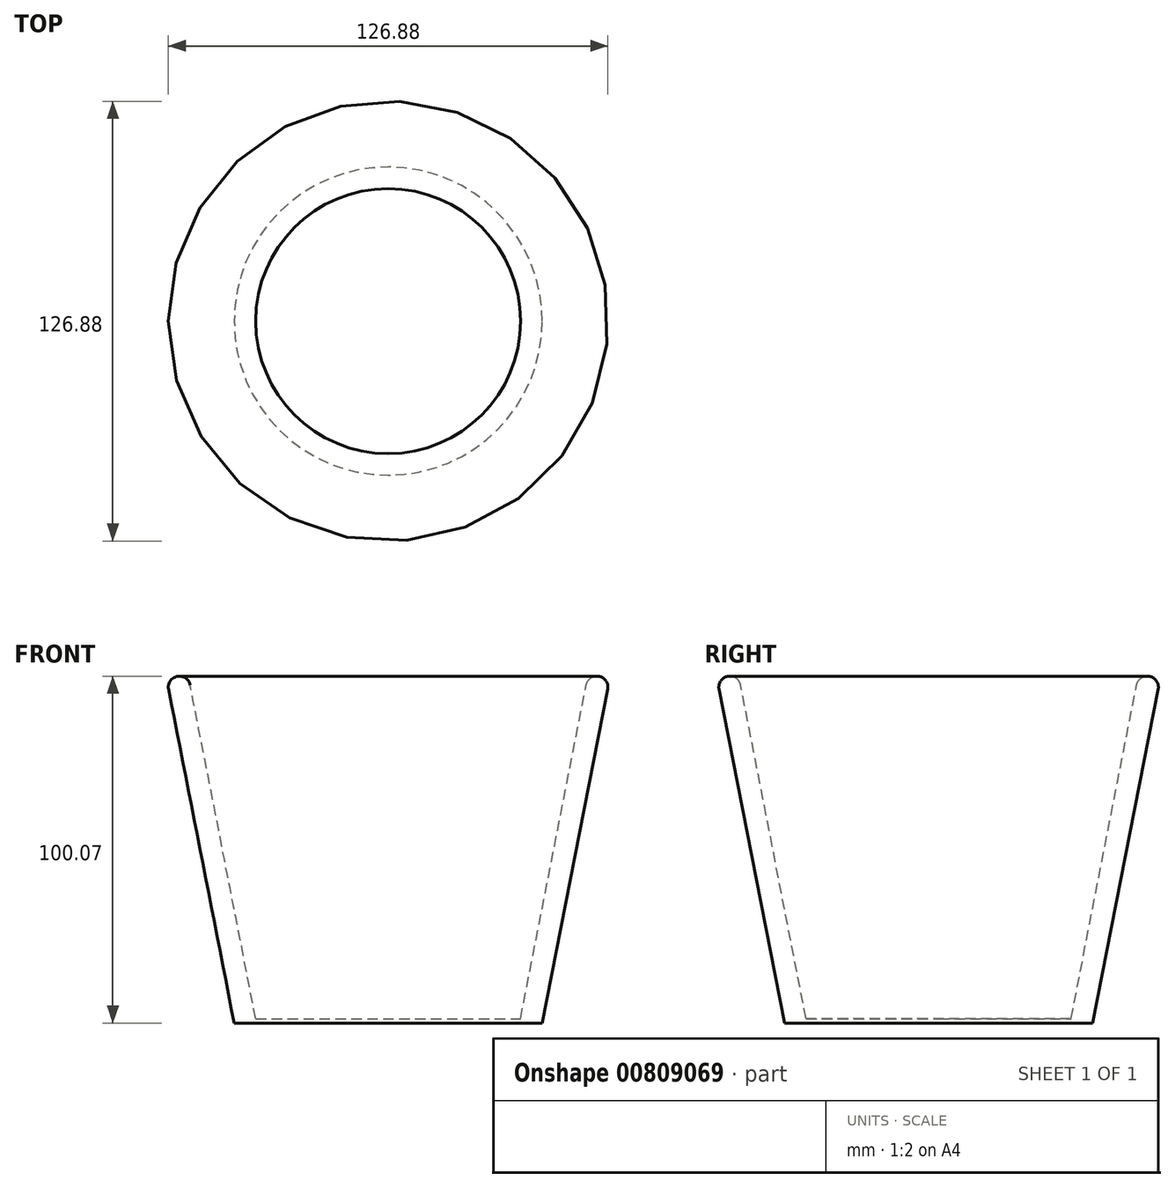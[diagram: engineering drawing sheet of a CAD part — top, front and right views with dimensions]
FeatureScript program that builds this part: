
annotation { "Feature Type Name" : "Feature", "Feature Type Description" : "" }
export const myFeature = defineFeature(function(context is Context, id is Id, definition is map)
    precondition{}
    {
        {
            var Q0;
            Q0=qCreatedBy(makeId("Right.planeOp"),FACE);
            var sketch = newSketch(context, id + "F0", { "sketchPlane" : qUnion([Q0])});
            skLineSegment(sketch, "E0.bottom", {"start": v(0, -51.38) * mm, "end": v(-44.45, -51.38) * mm});
            skLineSegment(sketch, "E0.top", {"start": v(0, -50.1) * mm, "end": v(-44.45, -50.1) * mm});
            skLineSegment(sketch, "E0.left", {"start": v(0, -51.38) * mm, "end": v(0, -50.1) * mm});
            skLineSegment(sketch, "E0.right", {"start": v(-44.45, -51.38) * mm, "end": v(-44.45, -50.1) * mm});
            skLineSegment(sketch, "E1", {"start": v(-44.45, -51.38) * mm, "end": v(-63.38, 44.9) * mm});
            skLineSegment(sketch, "E2", {"start": v(-63.38, 44.9) * mm, "end": v(-57.15, 46.13) * mm});
            skLineSegment(sketch, "E3", {"start": v(-57.15, 46.13) * mm, "end": v(-38.23, -50.1) * mm});
            skArc(sketch, "E4", {"start": v(-57.15, 46.13) * mm, "mid": v(-60.88, 48.63) * mm, "end": v(-63.38, 44.9) * mm});
            skSolve(sketch);
        }
        {
            var Q0;
            Q0=makeQuery(id+"F0.imprint","IMPRINT",FACE,{"disambiguationData":[TD([[makeQuery(id+"F0.imprint","IMPRINT",EDGE,{"derivedFrom":sQuery(id+"F0.wireOp",EDGE,"E2")}),1.0]])]});
            var Q1;
            {var subQ0=sQuery(id+"F0.wireOp",EDGE,"E0.right");Q1=makeQuery(id+"F0.imprint","IMPRINT",FACE,{"disambiguationData":[TD([[makeQuery(id+"F0.imprint","IMPRINT",EDGE,{"derivedFrom":subQ0}),1.0]])]});}
            var Q2;
            Q2=makeQuery(id+"F0.imprint","IMPRINT",FACE,{"disambiguationData":[TD([[makeQuery(id+"F0.imprint","IMPRINT",EDGE,{"derivedFrom":sQuery(id+"F0.wireOp",EDGE,"E0.bottom")}),-1.0]])]});
            var Q3;
            Q3=sQuery(id+"F0.wireOp",EDGE,"E0.left");
            revolve(context, id + "F1", {"surfaceOperationType" : NewSurfaceOperationType.NEW, "entities" : qUnion([Q0, Q1, Q2]), "axis" : qUnion([Q3]), "revolveType" : RevolveType.FULL});
        }
    });
